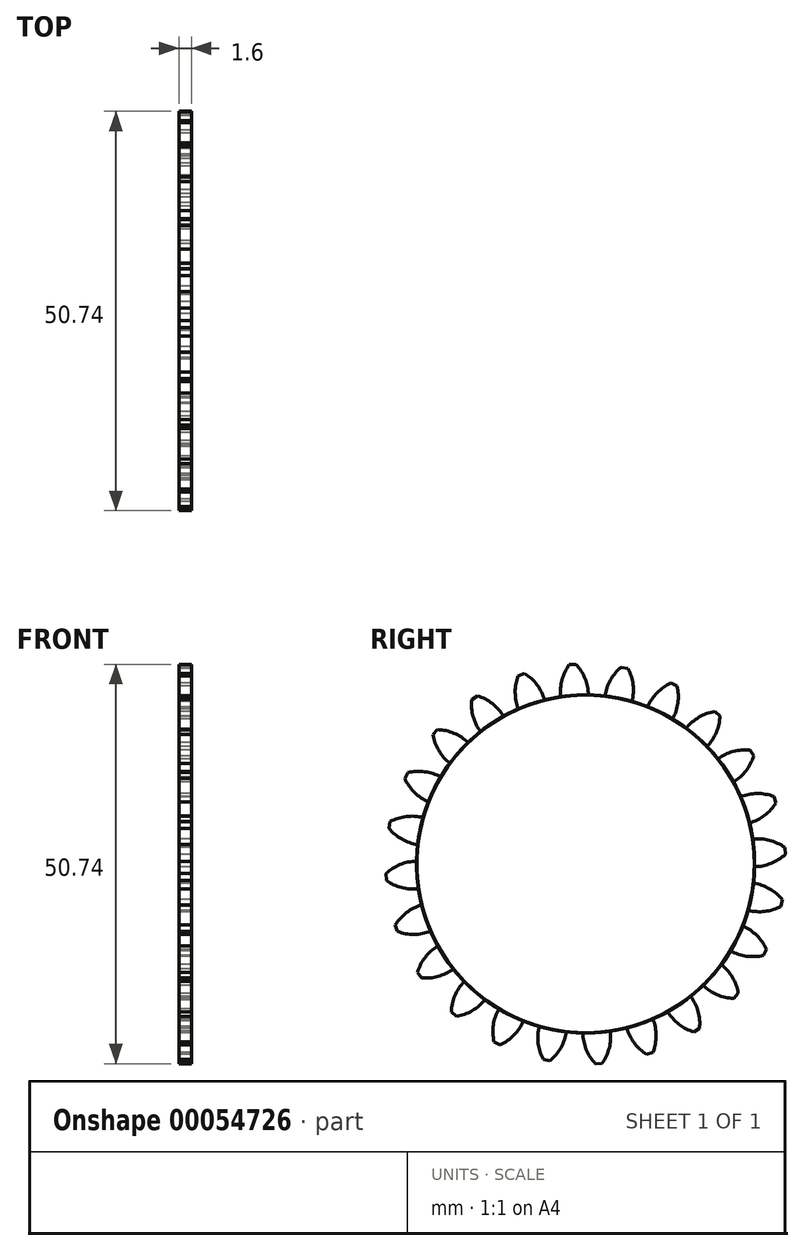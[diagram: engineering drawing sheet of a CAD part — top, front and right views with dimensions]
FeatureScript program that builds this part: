
annotation { "Feature Type Name" : "Feature", "Feature Type Description" : "" }
export const myFeature = defineFeature(function(context is Context, id is Id, definition is map)
    precondition{}
    {
        {
            var Q0;
            Q0=qCreatedBy(makeId("Right.planeOp"),FACE);
            var sketch = newSketch(context, id + "F0", { "sketchPlane" : qUnion([Q0])});
            skCircle(sketch, "E0", {"center": v(0, 0) * mm, "radius": 25.4 * mm, "construction": true});
            skCircle(sketch, "E1", {"center": v(0, 0) * mm, "radius": 21.46 * mm});
            skCircle(sketch, "E2", {"center": v(0, 0) * mm, "radius": 23.37 * mm, "construction": true});
            skLineSegment(sketch, "E3", {"start": v(0, 0) * mm, "end": v(0, 54.68) * mm, "construction": true});
            skLineSegment(sketch, "E4", {"start": v(0, 0) * mm, "end": v(-3.7, 56.38) * mm, "construction": true});
            skLineSegment(sketch, "E5", {"start": v(0, 23.37) * mm, "end": v(-45, 23.37) * mm, "construction": true});
            skPoint(sketch, "E5.startSnap0", {"position": v(0, 27.34) * mm});
            skLineSegment(sketch, "E6", {"start": v(0, 23.37) * mm, "end": v(-42.37, 7.95) * mm, "construction": true});
            skCircle(sketch, "E7", {"center": v(0, 23.37) * mm, "radius": 5.84 * mm, "construction": true});
            skCircle(sketch, "E8", {"center": v(-5.49, 21.37) * mm, "radius": 5.84 * mm, "construction": true});
            skArc(sketch, "E9", {"start": v(0.35, 21.46) * mm, "mid": v(-0.07, 23.56) * mm, "end": v(-1.23, 25.37) * mm});
            skArc(sketch, "E10.MirrorCS", {"start": v(-3.15, 21.23) * mm, "mid": v(-3, 23.37) * mm, "end": v(-2.09, 25.31) * mm});
            skLineSegment(sketch, "E11", {"start": v(-2.09, 25.31) * mm, "end": v(-1.23, 25.37) * mm});
            skSolve(sketch);
        }
        {
            var Q0;
            {var subQ0=sQuery(id+"F0.wireOp",EDGE,"E1");var subQ1=makeQuery(id+"F0.imprint","INTERSECT",VERTEX,{"derivedFrom":[subQ0,sQuery(id+"F0.wireOp",EDGE,"E9")]});Q0=makeQuery(id+"F0.imprint","IMPRINT",FACE,{"disambiguationData":[TD([[makeQuery(id+"F0.imprint","IMPRINT",EDGE,{"disambiguationData":[TD([[subQ1,-1.0]])],"derivedFrom":subQ0}),1.0]])]});}
            var Q1;
            {var subQ0=sQuery(id+"F0.wireOp",EDGE,"E9");Q1=makeQuery(id+"F0.imprint","IMPRINT",FACE,{"disambiguationData":[TD([[makeQuery(id+"F0.imprint","IMPRINT",EDGE,{"derivedFrom":subQ0}),1.0]])]});}
            extrude(context, id + "F1", {"entities" : qUnion([Q0, Q1]), "depth" : 1.6 * mm});
        }
        {
            var Q0;
            Q0=makeQuery(id+"F1.opExtrude","SWEPT_BODY",BODY,{"disambiguationData":[OSD([sQuery(id+"F0.wireOp",EDGE,"E1"),sQuery(id+"F0.wireOp",EDGE,"E9"),sQuery(id+"F0.wireOp",EDGE,"E10.MirrorCS"),sQuery(id+"F0.wireOp",EDGE,"E11")])]});
            var Q1;
            Q1=sQuery(id+"F0.wireOp",EDGE,"E1");
            circularPattern(context, id + "F2", {"entities" : qUnion([Q0]), "axis" : qUnion([Q1]), "angle" : 15 * degree, "instanceCount" : 24});
        }
    });
